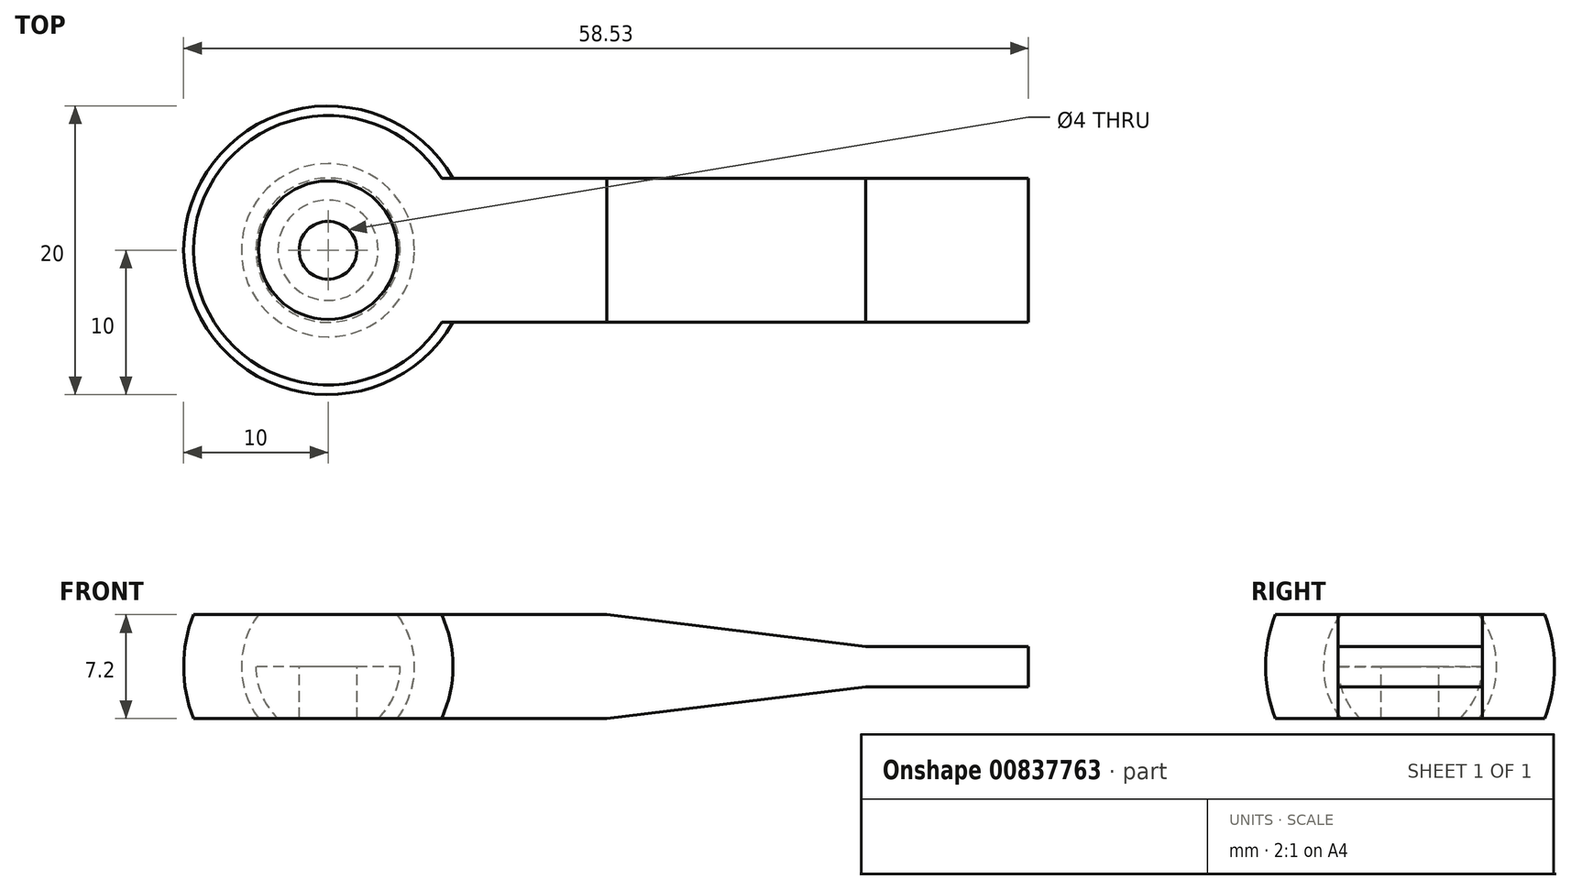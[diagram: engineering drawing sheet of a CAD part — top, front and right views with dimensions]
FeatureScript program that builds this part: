
annotation { "Feature Type Name" : "Feature", "Feature Type Description" : "" }
export const myFeature = defineFeature(function(context is Context, id is Id, definition is map)
    precondition{}
    {
        {
            var Q0;
            Q0=qCreatedBy(makeId("Front.planeOp"),FACE);
            var sketch = newSketch(context, id + "F0", { "sketchPlane" : qUnion([Q0])});
            skLineSegment(sketch, "E0.bottom", {"start": v(-9.08, 3.6) * mm, "end": v(10.03, 3.6) * mm, "construction": true});
            skLineSegment(sketch, "E0.top", {"start": v(-9.08, -3.6) * mm, "end": v(0, -3.6) * mm, "construction": true});
            skArc(sketch, "E1", {"start": v(9.33, 3.6) * mm, "mid": v(10, 0) * mm, "end": v(9.33, -3.6) * mm});
            skArc(sketch, "E2", {"start": v(4.8, 3.6) * mm, "mid": v(6, 0) * mm, "end": v(4.8, -3.6) * mm});
            skLineSegment(sketch, "E3", {"start": v(0, 0) * mm, "end": v(0, 5) * mm});
            skLineSegment(sketch, "E4", {"start": v(0, 0) * mm, "end": v(0, 3.6) * mm});
            skLineSegment(sketch, "E5", {"start": v(0, 0) * mm, "end": v(5, 0) * mm});
            skLineSegment(sketch, "E6", {"start": v(5, 0) * mm, "end": v(10, 0) * mm});
            skArc(sketch, "E7", {"start": v(3.48, 3.6) * mm, "mid": v(4.6, 1.95) * mm, "end": v(5, 0) * mm});
            skLineSegment(sketch, "E8", {"start": v(-10.67, 0) * mm, "end": v(14.32, 0) * mm, "construction": true});
            skLineSegment(sketch, "E9.MirrorCS", {"start": v(0, 0) * mm, "end": v(0, -3.6) * mm});
            skArc(sketch, "E10.MirrorCS", {"start": v(4.8, -3.6) * mm, "mid": v(6, 0) * mm, "end": v(4.8, 3.6) * mm});
            skArc(sketch, "E11.MirrorCS", {"start": v(3.48, -3.6) * mm, "mid": v(4.6, -1.95) * mm, "end": v(5, 0) * mm});
            skArc(sketch, "E12.MirrorCS", {"start": v(9.33, -3.6) * mm, "mid": v(10, 0) * mm, "end": v(9.33, 3.6) * mm});
            skPoint(sketch, "E13.orphan", {"position": v(0, -3.6) * mm});
            skLineSegment(sketch, "E14.trimOffspring", {"start": v(3.48, -3.6) * mm, "end": v(10.03, -3.6) * mm, "construction": true});
            skLineSegment(sketch, "E15", {"start": v(0, -3.6) * mm, "end": v(3.48, -3.6) * mm});
            skPoint(sketch, "E16.orphan", {"position": v(4.8, -3.6) * mm});
            skLineSegment(sketch, "E17.top", {"start": v(0, -3.6) * mm, "end": v(2, -3.6) * mm});
            skLineSegment(sketch, "E17.left", {"start": v(0, 3.6) * mm, "end": v(0, -3.6) * mm});
            skLineSegment(sketch, "E17.right", {"start": v(2, 3.6) * mm, "end": v(2, -3.6) * mm});
            skLineSegment(sketch, "E18", {"start": v(0, 11.52) * mm, "end": v(0, -13.17) * mm, "construction": true});
            skLineSegment(sketch, "E19", {"start": v(0, 3.6) * mm, "end": v(3.48, 3.6) * mm});
            skLineSegment(sketch, "E20", {"start": v(4.8, 3.6) * mm, "end": v(9.33, 3.6) * mm});
            skPoint(sketch, "E21.orphan", {"position": v(4, -3.6) * mm});
            skLineSegment(sketch, "E22.trimOffspring", {"start": v(4.8, -3.6) * mm, "end": v(9.33, -3.6) * mm});
            skPoint(sketch, "E23.middle", {"position": v(14.32, 0) * mm});
            skLineSegment(sketch, "E24.bottom", {"start": v(37.25, -1.4) * mm, "end": v(48.53, -1.4) * mm, "construction": true});
            skLineSegment(sketch, "E24.top", {"start": v(37.25, 1.4) * mm, "end": v(48.53, 1.4) * mm, "construction": true});
            skLineSegment(sketch, "E24.left", {"start": v(37.25, -1.4) * mm, "end": v(37.25, 1.4) * mm, "construction": true});
            skLineSegment(sketch, "E24.right", {"start": v(48.53, -1.4) * mm, "end": v(48.53, 1.4) * mm, "construction": true});
            skPoint(sketch, "E24.middle", {"position": v(42.89, 0) * mm});
            skLineSegment(sketch, "E25", {"start": v(19.31, -3.6) * mm, "end": v(37.25, -1.4) * mm});
            skLineSegment(sketch, "E26", {"start": v(37.25, 1.4) * mm, "end": v(19.31, 3.6) * mm});
            skLineSegment(sketch, "E27", {"start": v(37.25, -1.4) * mm, "end": v(48.53, -1.4) * mm});
            skLineSegment(sketch, "E28", {"start": v(48.53, -1.4) * mm, "end": v(48.53, 1.4) * mm});
            skLineSegment(sketch, "E29", {"start": v(48.53, 1.4) * mm, "end": v(37.25, 1.4) * mm});
            skLineSegment(sketch, "E30", {"start": v(19.31, 3.6) * mm, "end": v(7.07, 3.6) * mm});
            skLineSegment(sketch, "E31", {"start": v(7.07, 3.6) * mm, "end": v(7.07, -3.6) * mm});
            skLineSegment(sketch, "E32", {"start": v(7.07, -3.6) * mm, "end": v(19.31, -3.6) * mm});
            skSolve(sketch);
        }
        {
            var Q0;
            {var subQ0=sQuery(id+"F0.wireOp",EDGE,"E11.MirrorCS");Q0=makeQuery(id+"F0.imprint","IMPRINT",FACE,{"disambiguationData":[TD([[makeQuery(id+"F0.imprint","IMPRINT",EDGE,{"derivedFrom":subQ0}),1.0]])]});}
            var Q1;
            {var subQ0=sQuery(id+"F0.wireOp",EDGE,"E7");Q1=makeQuery(id+"F0.imprint","IMPRINT",FACE,{"disambiguationData":[TD([[makeQuery(id+"F0.imprint","IMPRINT",EDGE,{"derivedFrom":subQ0}),-1.0]])]});}
            var Q2;
            {var subQ5=sQuery(id+"F0.wireOp",EDGE,"E22.trimOffspring");Q2=makeQuery(id+"F0.imprint","IMPRINT",FACE,{"disambiguationData":[TD([[makeQuery(id+"F0.imprint","IMPRINT",EDGE,{"derivedFrom":subQ5}),1.0]])]});}
            var Q3;
            {var subQ5=sQuery(id+"F0.wireOp",EDGE,"E20");Q3=makeQuery(id+"F0.imprint","IMPRINT",FACE,{"disambiguationData":[TD([[makeQuery(id+"F0.imprint","IMPRINT",EDGE,{"derivedFrom":subQ5}),-1.0]])]});}
            var Q4;
            {var subQ0=sQuery(id+"F0.wireOp",EDGE,"E12.MirrorCS");var subQ1=sQuery(id+"F0.wireOp",EDGE,"E6");var subQ2=makeQuery(id+"F0.imprint","INTERSECT",VERTEX,{"derivedFrom":[subQ1,subQ0]});Q4=makeQuery(id+"F0.imprint","IMPRINT",FACE,{"disambiguationData":[TD([[makeQuery(id+"F0.imprint","IMPRINT",EDGE,{"disambiguationData":[TD([[subQ2,1.0]])],"derivedFrom":subQ1}),1.0]])]});}
            var Q5;
            {var subQ0=sQuery(id+"F0.wireOp",EDGE,"E12.MirrorCS");var subQ1=sQuery(id+"F0.wireOp",EDGE,"E6");var subQ2=makeQuery(id+"F0.imprint","INTERSECT",VERTEX,{"derivedFrom":[subQ1,subQ0]});Q5=makeQuery(id+"F0.imprint","IMPRINT",FACE,{"disambiguationData":[TD([[makeQuery(id+"F0.imprint","IMPRINT",EDGE,{"disambiguationData":[TD([[subQ2,1.0]])],"derivedFrom":subQ1}),-1.0]])]});}
            var Q6;
            Q6=sQuery(id+"F0.wireOp",EDGE,"E18");
            revolve(context, id + "F1", {"surfaceOperationType" : NewSurfaceOperationType.NEW, "entities" : qUnion([Q0, Q1, Q2, Q3, Q4, Q5]), "axis" : qUnion([Q6]), "revolveType" : RevolveType.FULL});
        }
        {
            var Q0;
            Q0=makeQuery(id+"F0.imprint","IMPRINT",FACE,{"disambiguationData":[TD([[makeQuery(id+"F0.imprint","IMPRINT",EDGE,{"derivedFrom":sQuery(id+"F0.wireOp",EDGE,"E25")}),1.0]])]});
            var Q1;
            {var subQ0=sQuery(id+"F0.wireOp",EDGE,"E12.MirrorCS");var subQ1=sQuery(id+"F0.wireOp",EDGE,"E6");var subQ2=makeQuery(id+"F0.imprint","INTERSECT",VERTEX,{"derivedFrom":[subQ1,subQ0]});Q1=makeQuery(id+"F0.imprint","IMPRINT",FACE,{"disambiguationData":[TD([[makeQuery(id+"F0.imprint","IMPRINT",EDGE,{"disambiguationData":[TD([[subQ2,1.0]])],"derivedFrom":subQ1}),1.0]])]});}
            var Q2;
            {var subQ0=sQuery(id+"F0.wireOp",EDGE,"E12.MirrorCS");var subQ1=sQuery(id+"F0.wireOp",EDGE,"E6");var subQ2=makeQuery(id+"F0.imprint","INTERSECT",VERTEX,{"derivedFrom":[subQ1,subQ0]});Q2=makeQuery(id+"F0.imprint","IMPRINT",FACE,{"disambiguationData":[TD([[makeQuery(id+"F0.imprint","IMPRINT",EDGE,{"disambiguationData":[TD([[subQ2,1.0]])],"derivedFrom":subQ1}),-1.0]])]});}
            extrude(context, id + "F2", {"entities" : qUnion([Q0, Q1, Q2]), "operationType" : NewBodyOperationType.ADD, "depth" : 5 * mm, "offsetDistance" : 25 * mm, "hasSecondDirection" : true, "secondDirectionOppositeDirection" : true, "secondDirectionDepth" : 5 * mm});
        }
    });
